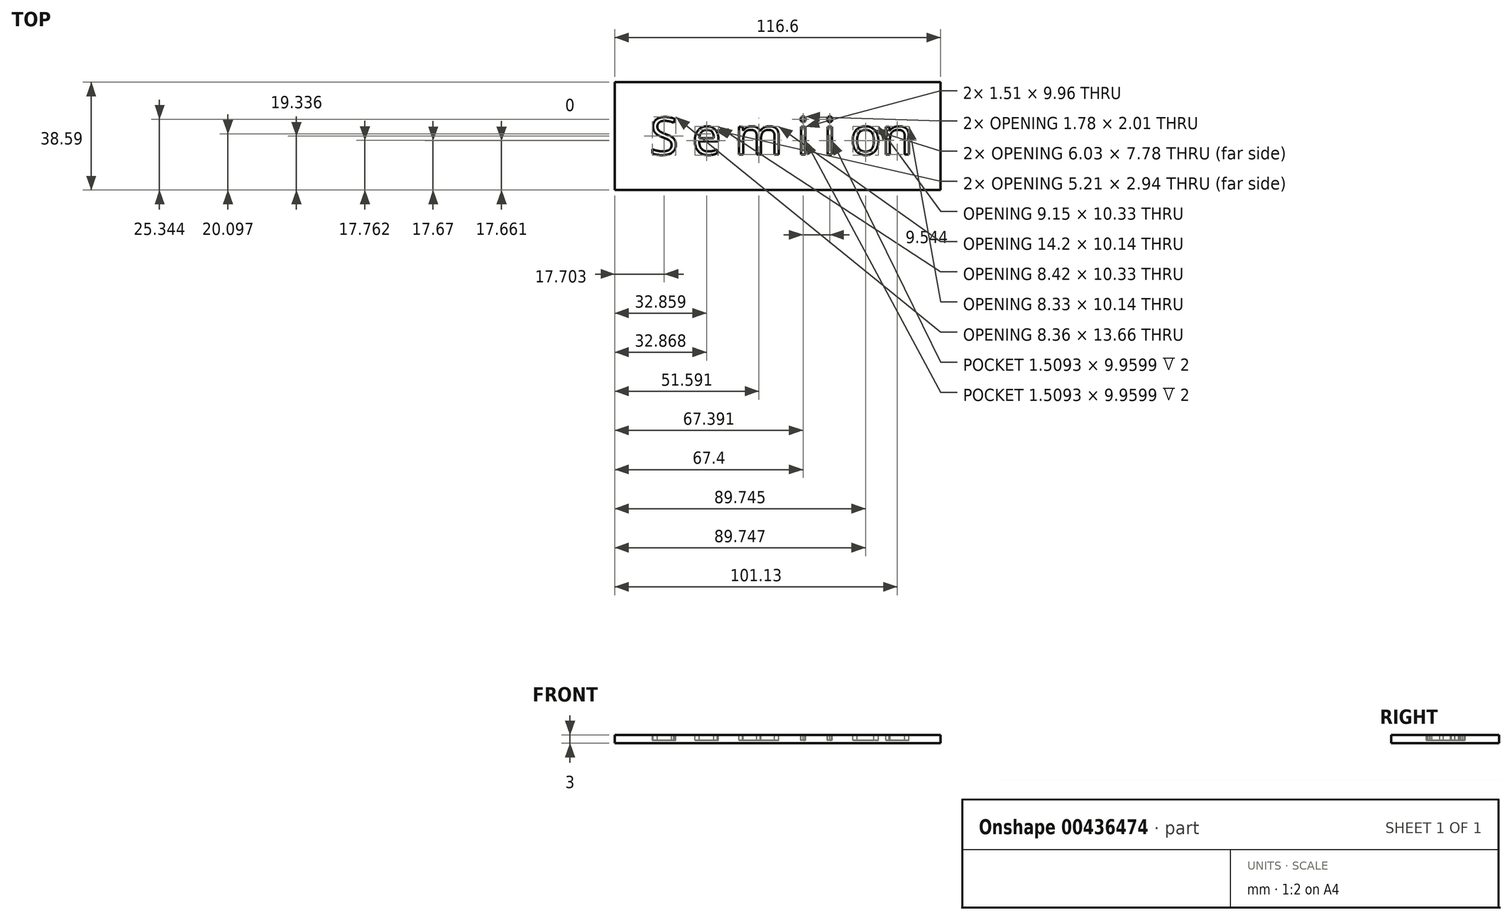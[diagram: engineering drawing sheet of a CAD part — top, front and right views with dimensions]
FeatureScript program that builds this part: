
annotation { "Feature Type Name" : "Feature", "Feature Type Description" : "" }
export const myFeature = defineFeature(function(context is Context, id is Id, definition is map)
    precondition{}
    {
        {
            var Q0;
            Q0=qCreatedBy(makeId("Top.planeOp"),FACE);
            var sketch = newSketch(context, id + "F0", { "sketchPlane" : qUnion([Q0])});
            skText(sketch, "E0", { "text": "S e m i i on", "fontName": "OpenSans-Regular.ttf"});
            const initialGuessF0  = {"E0": [-0.09382, 0, 1, 0, 0.0134]};
            skSetInitialGuess(sketch, initialGuessF0);
            skSolve(sketch);
        }
        {
            var Q0;
            Q0=qCreatedBy(makeId("Top.planeOp"),FACE);
            var sketch = newSketch(context, id + "F1", { "sketchPlane" : qUnion([Q0])});
            skLineSegment(sketch, "E1.bottom", {"start": v(-106.38, 25.9) * mm, "end": v(10.22, 25.9) * mm});
            skLineSegment(sketch, "E1.top", {"start": v(-106.38, -12.69) * mm, "end": v(10.22, -12.69) * mm});
            skLineSegment(sketch, "E1.left", {"start": v(-106.38, 25.9) * mm, "end": v(-106.38, -12.69) * mm});
            skLineSegment(sketch, "E1.right", {"start": v(10.22, 25.9) * mm, "end": v(10.22, -12.69) * mm});
            skSolve(sketch);
        }
        {
            var Q0;
            Q0=makeQuery(id+"F1.imprint","IMPRINT",FACE,{"disambiguationData":[TD([[makeQuery(id+"F1.imprint","IMPRINT",EDGE,{"derivedFrom":sQuery(id+"F1.wireOp",EDGE,"E1.bottom")}),-1.0]])]});
            extrude(context, id + "F2", {"entities" : qUnion([Q0]), "oppositeDirection" : true, "depth" : 3 * mm, "offsetDistance" : 25 * mm});
        }
        {
            var Q0;
            Q0 = qSketchRegion(id + "F0", true);
            extrude(context, id + "F3", {"entities" : qUnion([Q0]), "operationType" : NewBodyOperationType.REMOVE, "oppositeDirection" : true, "depth" : 2 * mm, "offsetDistance" : 25 * mm});
        }
        {
            var Q0;
            Q0 = qSketchRegion(id + "F0", true);
            extrude(context, id + "F4", {"entities" : qUnion([Q0]), "oppositeDirection" : true, "depth" : 2 * mm, "offsetDistance" : 25 * mm});
        }
    });
